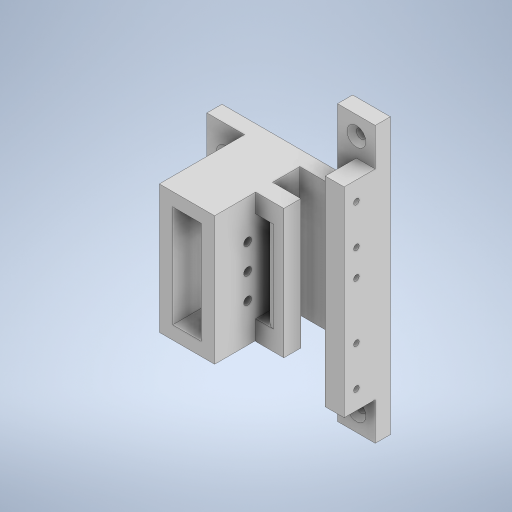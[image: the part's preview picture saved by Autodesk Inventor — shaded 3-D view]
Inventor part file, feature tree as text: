
AUTODESK INVENTOR PART (.ipt)
format: ipt  version: 2024 (Build 280153000, 153)  size: 472,576 bytes
history: native  units: mm
features: sketch x20, extrude x19, fillet x1, hole x1
ambient origin geometry x8: Origin, YZ Plane, XZ Plane, XY Plane, X Axis, Y Axis, Z Axis, Center Point
bodies: Solid1 (feature_tree)
feature tree (41):
  extrude  "Extrusion1"  Depth=45.2mm
  extrude  "Extrusion2"  Depth=7.0mm TaperAngle=0.0deg
  extrude  "Extrusion3"  Depth=7.0mm TaperAngle=0.0deg
  extrude  "Extrusion4"  Depth=10.0mm TaperAngle=0.0deg
  extrude  "Extrusion5"  Depth=20.0mm TaperAngle=0.0deg
  extrude  "Extrusion6"  Depth=54.2mm
  extrude  "Extrusion7"  Depth=45.2mm TaperAngle=0.0deg
  extrude  "Extrusion8"  Depth=20.0mm TaperAngle=0.0deg
  extrude  "Extrusion9"  Depth=15.0mm TaperAngle=0.0deg
  extrude  "Extrusion10"  TaperAngle=90.0deg  [1 undecoded]
  sketch  "Sketch11"  dims[d47=10.0mm d48=5.0mm]
  extrude  "Extrusion12"  Depth=5.0mm
  sketch  "Sketch13"  dims[d56=10.0mm d57=10.0mm]
  extrude  "Extrusion14"  Depth=7.0mm TaperAngle=0.0deg
  extrude  "Extrusion15"  Depth=10.0mm
  extrude  "Extrusion16"  Depth=4.5mm TaperAngle=0.0deg
  fillet  "Fillet2"  Radius=4.5mm
  extrude  "Extrusion17"  Depth=146.0mm
  extrude  "Extrusion18"  Depth=20.0mm
  extrude  "Extrusion19"  Depth=10.0mm
  extrude  "Extrusion20"  Depth=10.0mm
  hole  "Hole1"  [1 undecoded]
  extrude  "Extrusion21"  Depth=8.0mm
  sketch  "Sketch1"  dims[d0=54.2mm d1=45.2mm]
  sketch  "Sketch2"  dims[d2=15.3mm d3=0.0mm d4=7.0mm d5=0.0mm]
  sketch  "Sketch3"  dims[d6=7.0mm d7=0.0mm d8=7.0mm d9=0.0mm]
  sketch  "Sketch4"  dims[d10=7.0mm d11=0.0mm d12=10.0mm d13=0.0mm]
  sketch  "Sketch5"  dims[d14=10.0mm d15=20.0mm d16=0.0mm]
  sketch  "Sketch6"  dims[d17=15.2mm d18=54.2mm]
  sketch  "Sketch7"  dims[d19=45.2mm d20=0.0mm d34=39.25mm d35=0.0mm]
  sketch  "Sketch8"  dims[d36=10.0mm d37=20.0mm d38=0.0mm]
  sketch  "Sketch9"  dims[d42=9.0mm d43=15.0mm d44=0.0mm]
  sketch  "Sketch10"  dims[d45=10.0mm d46=90.0deg]
  sketch  "Sketch12"  dims[d52=7.0mm d53=0.0mm d54=7.0mm d55=0.0mm]
  sketch  "Sketch14"  dims[d58=90.0deg d59=9.75mm d60=0.0mm d61=4.5mm]
  sketch  "Sketch15"  dims[d62=10.0mm d63=146.0mm]
  sketch  "Sketch16"  dims[d64=20.0mm d65=0.0mm d66=20.0mm]
  sketch  "Sketch17"  dims[d67=20.0mm d68=10.0mm]
  sketch  "Sketch18"  dims[d69=20.0mm d70=0.0mm d71=10.0mm]
  sketch  "Sketch19"  dims[d72=21.0mm d73=10.0mm]
  sketch  "Sketch21"  dims[d74=21.0mm d75=14.0mm d76=3.0mm d77=3.0mm d78=3.0mm d79=3.0mm d80=3.0mm d81=5.0mm d82=20.0mm d83=0.0mm d84=1.5mm d85=0.0mm d86=10.0mm d87=10.0mm d88=15.0mm d89=15.0mm d90=5.0mm d91=6.0mm d92=10.0mm d93=2.0mm d94=90.0deg d95=8.0mm d96=20.594885mm d97=2.0mm d98=171.5mm d99=0.0mm]
note: 2 required parameter values undecoded (feature->parameter linkage not recoverable at this tier; creation-order binding heuristic only, values carry confidence <= 0.55)
